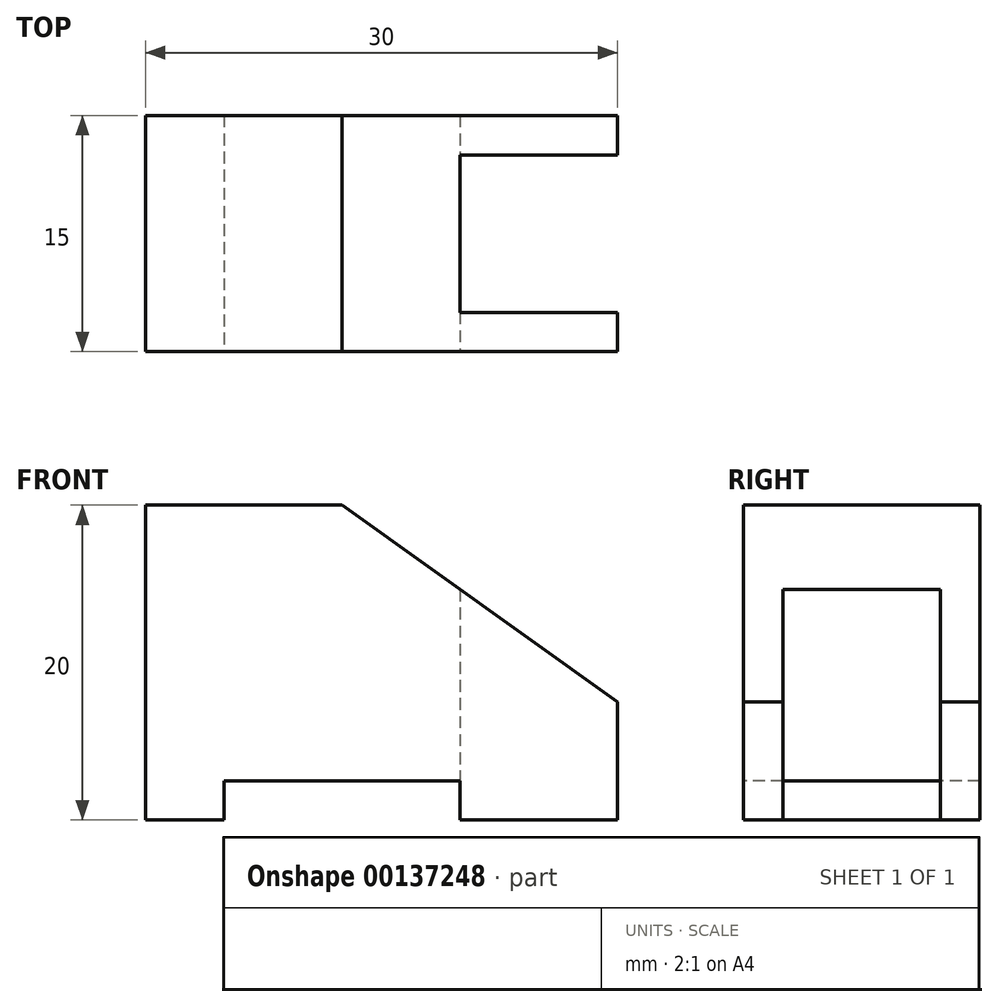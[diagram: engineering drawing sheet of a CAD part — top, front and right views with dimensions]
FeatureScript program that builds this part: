
annotation { "Feature Type Name" : "Feature", "Feature Type Description" : "" }
export const myFeature = defineFeature(function(context is Context, id is Id, definition is map)
    precondition{}
    {
        {
            var Q0;
            Q0=qCreatedBy(makeId("Top.planeOp"),FACE);
            var sketch = newSketch(context, id + "F0", { "sketchPlane" : qUnion([Q0])});
            skLineSegment(sketch, "E0", {"start": v(0, 0) * mm, "end": v(0, 15) * mm});
            skLineSegment(sketch, "E1", {"start": v(0, 15) * mm, "end": v(30, 15) * mm});
            skLineSegment(sketch, "E2", {"start": v(30, 15) * mm, "end": v(30, 12.5) * mm});
            skLineSegment(sketch, "E3", {"start": v(30, 12.5) * mm, "end": v(20, 12.5) * mm});
            skLineSegment(sketch, "E4", {"start": v(20, 12.5) * mm, "end": v(20, 2.5) * mm});
            skLineSegment(sketch, "E5", {"start": v(20, 2.5) * mm, "end": v(30, 2.5) * mm});
            skLineSegment(sketch, "E6", {"start": v(30, 2.5) * mm, "end": v(30, 0) * mm});
            skLineSegment(sketch, "E7", {"start": v(30, 0) * mm, "end": v(0, 0) * mm});
            skSolve(sketch);
        }
        {
            var Q0;
            Q0 = qSketchRegion(id + "F0", true);
            extrude(context, id + "F1", {"entities" : qUnion([Q0]), "depth" : 20 * mm});
        }
        {
            var Q0;
            Q0=makeQuery(id+"F1.opExtrude","SWEPT_FACE",FACE,{"disambiguationData":[OSD([sQuery(id+"F0.wireOp",EDGE,"E7")])]});
            var sketch = newSketch(context, id + "F2", { "sketchPlane" : qUnion([Q0])});
            skLineSegment(sketch, "E8", {"start": v(5, 0) * mm, "end": v(20, 0) * mm});
            skLineSegment(sketch, "E9", {"start": v(20, 0) * mm, "end": v(20, 2.5) * mm});
            skLineSegment(sketch, "E10", {"start": v(20, 2.5) * mm, "end": v(5, 2.5) * mm});
            skLineSegment(sketch, "E11", {"start": v(5, 2.5) * mm, "end": v(5, 0) * mm});
            skLineSegment(sketch, "E12", {"start": v(30, 7.5) * mm, "end": v(12.5, 20) * mm});
            skLineSegment(sketch, "E13", {"start": v(12.5, 20) * mm, "end": v(30, 20) * mm});
            skLineSegment(sketch, "E14", {"start": v(30, 20) * mm, "end": v(30, 7.5) * mm});
            skSolve(sketch);
        }
        {
            var Q0;
            Q0 = qSketchRegion(id + "F2", true);
            extrude(context, id + "F3", {"entities" : qUnion([Q0]), "operationType" : NewBodyOperationType.REMOVE, "endBound" : BoundingType.THROUGH_ALL, "oppositeDirection" : true, "depth" : 25 * mm});
        }
    });
